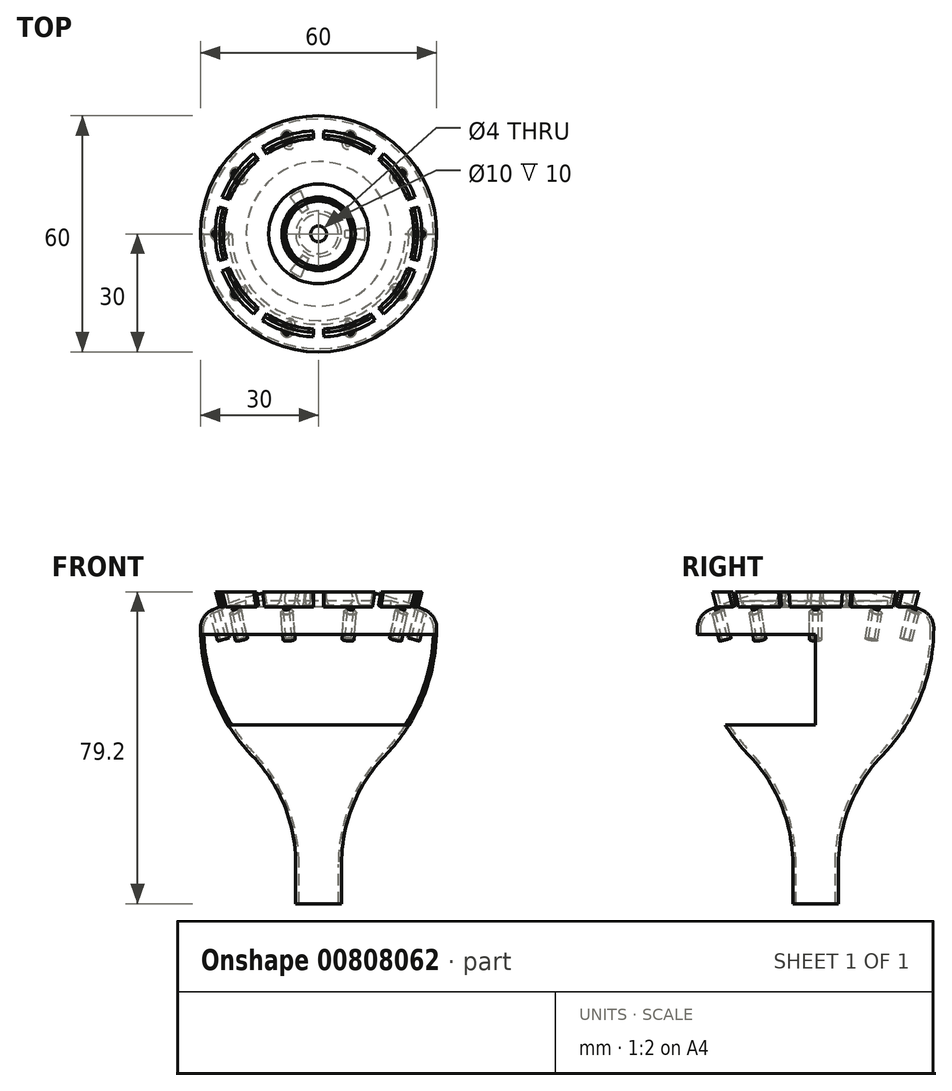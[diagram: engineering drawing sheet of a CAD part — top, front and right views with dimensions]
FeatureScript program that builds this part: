
annotation { "Feature Type Name" : "Feature", "Feature Type Description" : "" }
export const myFeature = defineFeature(function(context is Context, id is Id, definition is map)
    precondition{}
    {
        {
            var Q0;
            Q0=qCreatedBy(makeId("Front.planeOp"),FACE);
            var sketch = newSketch(context, id + "F0", { "sketchPlane" : qUnion([Q0])});
            skArc(sketch, "E0", {"start": v(27.06, 29.16) * mm, "mid": v(18.3, 32.4) * mm, "end": v(9.16, 34.35) * mm});
            skArc(sketch, "E1", {"start": v(30, 24.6) * mm, "mid": v(29.2, 27.32) * mm, "end": v(27.06, 29.16) * mm});
            skArc(sketch, "E2", {"start": v(16.98, -7.7) * mm, "mid": v(8.7, -20.49) * mm, "end": v(5.8, -35.44) * mm});
            skArc(sketch, "E3", {"start": v(16.98, -7.7) * mm, "mid": v(26.62, 7.2) * mm, "end": v(30, 24.6) * mm});
            skLineSegment(sketch, "E4", {"start": v(5.8, -35.44) * mm, "end": v(5.8, -45.44) * mm});
            skArc(sketch, "E5", {"start": v(26.73, 28.43) * mm, "mid": v(22.6, 30.13) * mm, "end": v(18.37, 31.54) * mm});
            skArc(sketch, "E6", {"start": v(29.2, 24.6) * mm, "mid": v(28.53, 26.88) * mm, "end": v(26.73, 28.43) * mm});
            skArc(sketch, "E7", {"start": v(16.4, -7.15) * mm, "mid": v(25.88, 7.49) * mm, "end": v(29.2, 24.6) * mm});
            skArc(sketch, "E8", {"start": v(16.4, -7.15) * mm, "mid": v(7.96, -20.19) * mm, "end": v(5, -35.44) * mm});
            skLineSegment(sketch, "E9", {"start": v(9.16, 34.35) * mm, "end": v(9.94, 31.46) * mm});
            skLineSegment(sketch, "E10", {"start": v(18.37, 30) * mm, "end": v(18.37, 31.54) * mm});
            skLineSegment(sketch, "E11", {"start": v(8.1, 34.5) * mm, "end": v(8.63, 32.48) * mm});
            skLineSegment(sketch, "E12", {"start": v(6.72, 30) * mm, "end": v(3.97, 30) * mm});
            skLineSegment(sketch, "E13", {"start": v(2, 31.97) * mm, "end": v(2, 34.97) * mm});
            skArc(sketch, "E14.trimOffspring", {"start": v(8.1, 34.5) * mm, "mid": v(5.05, 34.8) * mm, "end": v(2, 34.97) * mm});
            skLineSegment(sketch, "E15", {"start": v(11.85, 30) * mm, "end": v(18.37, 30) * mm});
            skLineSegment(sketch, "E16", {"start": v(5, -35.44) * mm, "end": v(5, -45.44) * mm});
            skLineSegment(sketch, "E17", {"start": v(5.8, -45.44) * mm, "end": v(5, -45.44) * mm});
            skLineSegment(sketch, "E18", {"start": v(0, 36.3) * mm, "end": v(0, 3.82) * mm});
            skArc(sketch, "E19", {"start": v(9.94, 31.46) * mm, "mid": v(10.65, 30.4) * mm, "end": v(11.85, 30) * mm});
            skArc(sketch, "E20", {"start": v(6.72, 30) * mm, "mid": v(8.3, 30.76) * mm, "end": v(8.63, 32.48) * mm});
            skPoint(sketch, "E21.orphan", {"position": v(9.3, 30) * mm});
            skArc(sketch, "E22", {"start": v(2, 31.97) * mm, "mid": v(2.58, 30.57) * mm, "end": v(3.97, 30) * mm});
            skSolve(sketch);
        }
        {
            var Q0;
            Q0 = qSketchRegion(id + "F0", true);
            var Q1;
            Q1=sQuery(id+"F0.wireOp",EDGE,"E18");
            revolve(context, id + "F1", {"surfaceOperationType" : NewSurfaceOperationType.NEW, "entities" : qUnion([Q0]), "axis" : qUnion([Q1]), "revolveType" : RevolveType.FULL});
        }
        {
            var Q0;
            Q0=qCreatedBy(makeId("Top.planeOp"),FACE);
            var sketch = newSketch(context, id + "F2", { "sketchPlane" : qUnion([Q0])});
            skLineSegment(sketch, "E23.bottom", {"start": v(56.28, 0) * mm, "end": v(-65.01, 0) * mm});
            skLineSegment(sketch, "E23.top", {"start": v(56.28, -48.28) * mm, "end": v(-65.01, -48.28) * mm});
            skLineSegment(sketch, "E23.left", {"start": v(56.28, 0) * mm, "end": v(56.28, -48.28) * mm});
            skLineSegment(sketch, "E23.right", {"start": v(-65.01, 0) * mm, "end": v(-65.01, -48.28) * mm});
            skSolve(sketch);
        }
        {
            var Q0;
            Q0=makeQuery(id+"F2.imprint","IMPRINT",FACE,{"disambiguationData":[TD([[makeQuery(id+"F2.imprint","IMPRINT",EDGE,{"derivedFrom":sQuery(id+"F2.wireOp",EDGE,"E23.bottom")}),1.0]])]});
            extrude(context, id + "F3", {"entities" : qUnion([Q0]), "operationType" : NewBodyOperationType.REMOVE, "depth" : 23 * mm, "offsetDistance" : 25 * mm});
        }
        {
            var Q0;
            Q0=qCreatedBy(makeId("Front.planeOp"),FACE);
            var sketch = newSketch(context, id + "F4", { "sketchPlane" : qUnion([Q0])});
            skArc(sketch, "E24.0", {"start": v(9.94, 31.46) * mm, "mid": v(10.65, 30.4) * mm, "end": v(11.85, 30) * mm});
            skArc(sketch, "E25.0", {"start": v(6.72, 30) * mm, "mid": v(8.3, 30.76) * mm, "end": v(8.63, 32.48) * mm});
            skLineSegment(sketch, "E26.0", {"start": v(9.16, 34.35) * mm, "end": v(9.94, 31.46) * mm});
            skLineSegment(sketch, "E27.0", {"start": v(8.1, 34.5) * mm, "end": v(8.63, 32.48) * mm});
            skLineSegment(sketch, "E28", {"start": v(8.1, 34.5) * mm, "end": v(9.16, 34.35) * mm});
            skLineSegment(sketch, "E29", {"start": v(6.72, 30) * mm, "end": v(11.85, 30) * mm});
            skSolve(sketch);
        }
        {
            var Q0;
            Q0 = qSketchRegion(id + "F4", true);
            var Q1;
            Q1=makeQuery(id+"F1.opRevolve","SWEPT_FACE",FACE,{"disambiguationData":[OSD([sQuery(id+"F0.wireOp",EDGE,"E13")])]});
            revolve(context, id + "F5", {"surfaceOperationType" : NewSurfaceOperationType.NEW, "entities" : qUnion([Q0]), "axis" : qUnion([Q1]), "revolveType" : RevolveType.SYMMETRIC, "angle" : 15 * degree});
        }
        {
            var Q0;
            Q0=makeQuery(id+"F5.opRevolve","SWEPT_BODY",BODY,{"disambiguationData":[OSD([sQuery(id+"F4.wireOp",EDGE,"E24.0"),sQuery(id+"F4.wireOp",EDGE,"E25.0"),sQuery(id+"F4.wireOp",EDGE,"E26.0"),sQuery(id+"F4.wireOp",EDGE,"E27.0"),sQuery(id+"F4.wireOp",EDGE,"E28"),sQuery(id+"F4.wireOp",EDGE,"E29")])]});
            var Q1;
            Q1=makeQuery(id+"F1.opRevolve","SWEPT_FACE",FACE,{"disambiguationData":[OSD([sQuery(id+"F0.wireOp",EDGE,"E13")])]});
            circularPattern(context, id + "F6", {"entities" : qUnion([Q0]), "axis" : qUnion([Q1]), "angle" : 360 * degree, "instanceCount" : 3, "equalSpace" : true});
        }
        {
            var Q0;
            Q0=qCreatedBy(makeId("Front.planeOp"),FACE);
            var sketch = newSketch(context, id + "F7", { "sketchPlane" : qUnion([Q0])});
            skLineSegment(sketch, "E30", {"start": v(27.65, 31.79) * mm, "end": v(24.5, 20.01) * mm});
            skLineSegment(sketch, "E31", {"start": v(24.5, 20.01) * mm, "end": v(23.77, 20.2) * mm});
            skLineSegment(sketch, "E32", {"start": v(23.77, 20.2) * mm, "end": v(26.92, 31.98) * mm});
            skLineSegment(sketch, "E33", {"start": v(26.92, 31.98) * mm, "end": v(27.65, 31.79) * mm});
            skSolve(sketch);
        }
        {
            var Q0;
            Q0=makeQuery(id+"F7.imprint","IMPRINT",FACE,{"disambiguationData":[TD([[makeQuery(id+"F7.imprint","IMPRINT",EDGE,{"derivedFrom":sQuery(id+"F7.wireOp",EDGE,"E30")}),-1.0]])]});
            var Q1;
            Q1=sQuery(id+"F7.wireOp",EDGE,"E32");
            revolve(context, id + "F8", {"surfaceOperationType" : NewSurfaceOperationType.NEW, "entities" : qUnion([Q0]), "axis" : qUnion([Q1]), "revolveType" : RevolveType.FULL, "oppositeDirection" : true});
        }
        {
            var Q0;
            Q0=makeQuery(id+"F8.opRevolve","SWEPT_BODY",BODY,{"disambiguationData":[OSD([sQuery(id+"F7.wireOp",EDGE,"E30"),sQuery(id+"F7.wireOp",EDGE,"E31"),sQuery(id+"F7.wireOp",EDGE,"E32"),sQuery(id+"F7.wireOp",EDGE,"E33")])]});
            var Q1;
            Q1=makeQuery(id+"F1.opRevolve","SWEPT_FACE",FACE,{"disambiguationData":[OSD([sQuery(id+"F0.wireOp",EDGE,"E13")])]});
            circularPattern(context, id + "F9", {"operationType" : NewBodyOperationType.REMOVE, "entities" : qUnion([Q0]), "axis" : qUnion([Q1]), "angle" : 360 * degree, "instanceCount" : 10, "equalSpace" : true});
        }
        {
            var Q0;
            Q0=qCreatedBy(makeId("Front.planeOp"),FACE);
            var sketch = newSketch(context, id + "F10", { "sketchPlane" : qUnion([Q0])});
            skLineSegment(sketch, "E34", {"start": v(27.64, 28.68) * mm, "end": v(26.87, 28.89) * mm});
            skLineSegment(sketch, "E35", {"start": v(26.87, 28.89) * mm, "end": v(24.9, 21.5) * mm});
            skLineSegment(sketch, "E36", {"start": v(24.9, 21.5) * mm, "end": v(25.67, 21.3) * mm});
            skLineSegment(sketch, "E37", {"start": v(25.67, 21.3) * mm, "end": v(27.64, 28.68) * mm});
            skSolve(sketch);
        }
        {
            var Q0;
            Q0=makeQuery(id+"F10.imprint","IMPRINT",FACE,{"disambiguationData":[TD([[makeQuery(id+"F10.imprint","IMPRINT",EDGE,{"derivedFrom":sQuery(id+"F10.wireOp",EDGE,"E34")}),1.0]])]});
            var Q1;
            Q1=makeQuery(id+"F9.boolean.opBoolean","COPY",FACE,{"derivedFrom":makeQuery(id+"F8.opRevolve","SWEPT_FACE",FACE,{"disambiguationData":[OSD([sQuery(id+"F7.wireOp",EDGE,"E30")])]})});
            revolve(context, id + "F11", {"surfaceOperationType" : NewSurfaceOperationType.NEW, "entities" : qUnion([Q0]), "axis" : qUnion([Q1]), "revolveType" : RevolveType.FULL});
        }
        {
            var Q0;
            Q0=makeQuery(id+"F11.opRevolve","SWEPT_BODY",BODY,{"disambiguationData":[OSD([sQuery(id+"F10.wireOp",EDGE,"E34"),sQuery(id+"F10.wireOp",EDGE,"E35"),sQuery(id+"F10.wireOp",EDGE,"E36"),sQuery(id+"F10.wireOp",EDGE,"E37")])]});
            var Q1;
            Q1=makeQuery(id+"F1.opRevolve","SWEPT_FACE",FACE,{"disambiguationData":[OSD([sQuery(id+"F0.wireOp",EDGE,"E13")])]});
            circularPattern(context, id + "F12", {"operationType" : NewBodyOperationType.ADD, "entities" : qUnion([Q0]), "axis" : qUnion([Q1]), "angle" : 360 * degree, "instanceCount" : 10, "equalSpace" : true});
        }
        {
            var Q0;
            Q0=qCreatedBy(makeId("Front.planeOp"),FACE);
            var sketch = newSketch(context, id + "F13", { "sketchPlane" : qUnion([Q0])});
            skArc(sketch, "E38.0", {"start": v(25.2, 29.97) * mm, "mid": v(24.7, 30.17) * mm, "end": v(24.2, 30.38) * mm});
            skLineSegment(sketch, "E39", {"start": v(25.2, 29.97) * mm, "end": v(26.44, 34.6) * mm});
            skLineSegment(sketch, "E40", {"start": v(26.44, 34.6) * mm, "end": v(25.4, 34.87) * mm});
            skLineSegment(sketch, "E41", {"start": v(25.4, 34.87) * mm, "end": v(24.2, 30.38) * mm});
            skPoint(sketch, "E42.orphan", {"position": v(27.06, 29.16) * mm});
            skSolve(sketch);
        }
        {
            var Q0;
            Q0=makeQuery(id+"F13.imprint","IMPRINT",FACE,{"disambiguationData":[TD([[makeQuery(id+"F13.imprint","IMPRINT",EDGE,{"derivedFrom":sQuery(id+"F13.wireOp",EDGE,"E38.0")}),-1.0]])]});
            var Q1;
            Q1=makeQuery(id+"F1.opRevolve","SWEPT_FACE",FACE,{"disambiguationData":[OSD([sQuery(id+"F0.wireOp",EDGE,"E13")])]});
            revolve(context, id + "F14", {"surfaceOperationType" : NewSurfaceOperationType.NEW, "entities" : qUnion([Q0]), "axis" : qUnion([Q1]), "revolveType" : RevolveType.SYMMETRIC, "angle" : 30 * degree});
        }
        {
            var Q0;
            Q0=makeQuery(id+"F14.opRevolve","SWEPT_BODY",BODY,{"disambiguationData":[OSD([sQuery(id+"F13.wireOp",EDGE,"E38.0"),sQuery(id+"F13.wireOp",EDGE,"E39"),sQuery(id+"F13.wireOp",EDGE,"E40"),sQuery(id+"F13.wireOp",EDGE,"E41")])]});
            var Q1;
            Q1=makeQuery(id+"F1.opRevolve","SWEPT_FACE",FACE,{"disambiguationData":[OSD([sQuery(id+"F0.wireOp",EDGE,"E13")])]});
            circularPattern(context, id + "F15", {"operationType" : NewBodyOperationType.ADD, "entities" : qUnion([Q0]), "axis" : qUnion([Q1]), "angle" : 360 * degree, "instanceCount" : 10, "equalSpace" : true});
        }
        {
            var Q0;
            Q0=qCreatedBy(makeId("Front.planeOp"),FACE);
            var sketch = newSketch(context, id + "F16", { "sketchPlane" : qUnion([Q0])});
            skLineSegment(sketch, "E43.bottom", {"start": v(0, 45.95) * mm, "end": v(29.1, 45.95) * mm});
            skLineSegment(sketch, "E43.top", {"start": v(0, 33.76) * mm, "end": v(29.1, 33.76) * mm});
            skLineSegment(sketch, "E43.left", {"start": v(0, 45.95) * mm, "end": v(0, 33.76) * mm});
            skLineSegment(sketch, "E43.right", {"start": v(29.1, 45.95) * mm, "end": v(29.1, 33.76) * mm});
            skSolve(sketch);
        }
        {
            var Q0;
            Q0=makeQuery(id+"F16.imprint","IMPRINT",FACE,{"disambiguationData":[TD([[makeQuery(id+"F16.imprint","IMPRINT",EDGE,{"derivedFrom":sQuery(id+"F16.wireOp",EDGE,"E43.bottom")}),-1.0]])]});
            var Q1;
            Q1=sQuery(id+"F16.wireOp",EDGE,"E43.left");
            revolve(context, id + "F17", {"operationType" : NewBodyOperationType.REMOVE, "surfaceOperationType" : NewSurfaceOperationType.NEW, "entities" : qUnion([Q0]), "axis" : qUnion([Q1]), "revolveType" : RevolveType.FULL, "oppositeDirection" : true});
        }
    });
